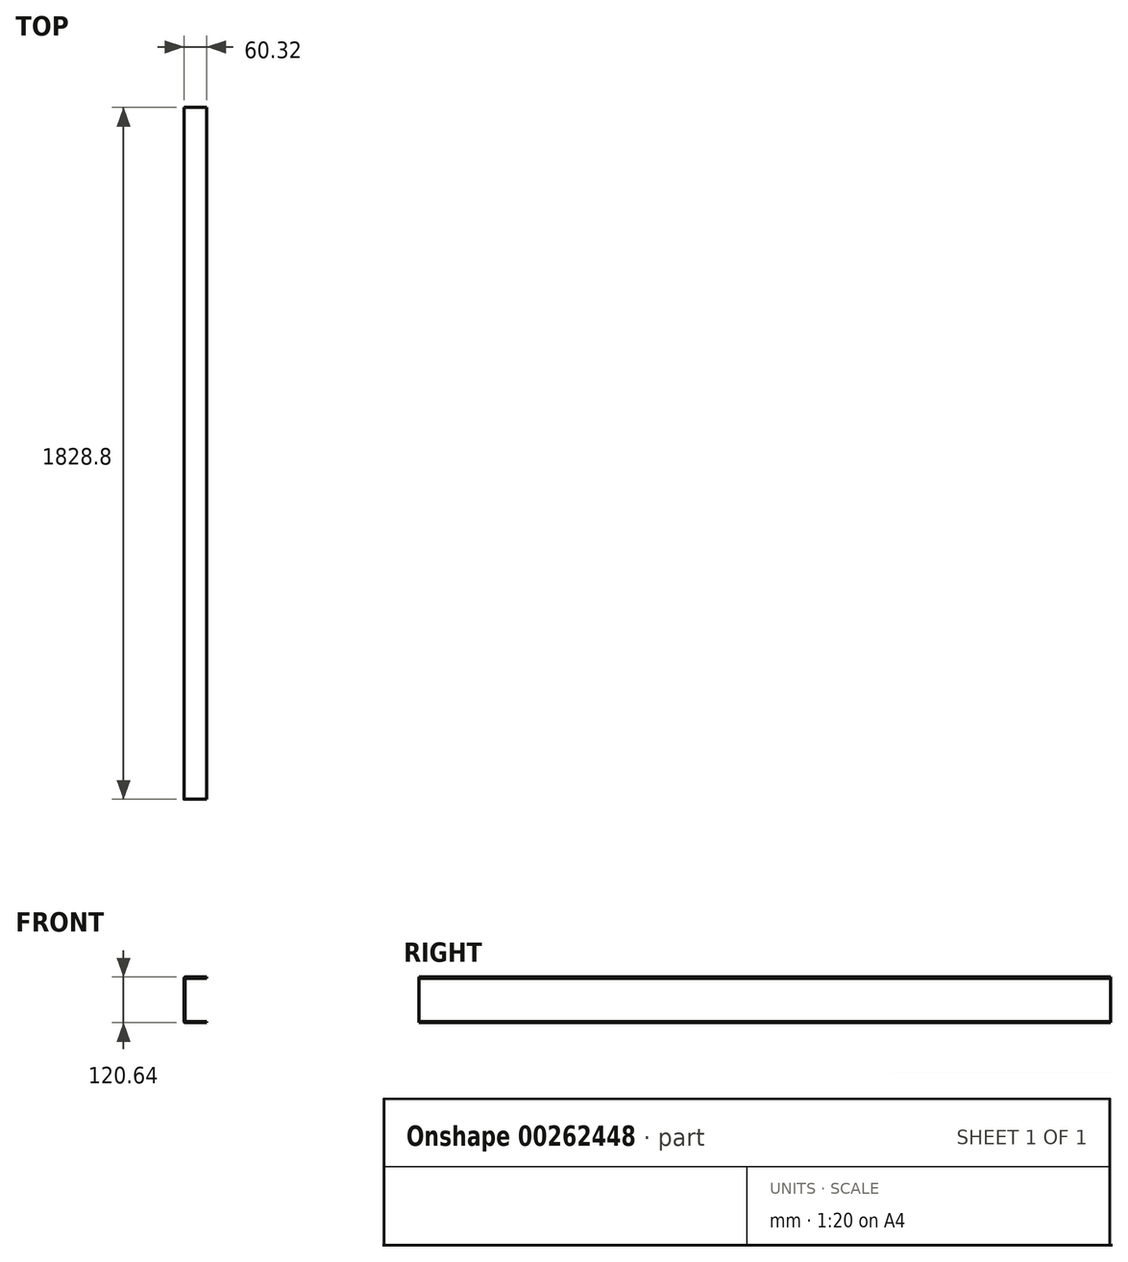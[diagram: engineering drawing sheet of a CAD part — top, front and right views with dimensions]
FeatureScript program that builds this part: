
annotation { "Feature Type Name" : "Feature", "Feature Type Description" : "" }
export const myFeature = defineFeature(function(context is Context, id is Id, definition is map)
    precondition{}
    {
        {
            var Q0;
            Q0=qCreatedBy(makeId("Front.planeOp"),FACE);
            var sketch = newSketch(context, id + "F0", { "sketchPlane" : qUnion([Q0])});
            skLineSegment(sketch, "E0.bottom", {"start": v(30.16, 60.33) * mm, "end": v(-26.99, 60.33) * mm});
            skLineSegment(sketch, "E0.top", {"start": v(30.16, -60.32) * mm, "end": v(-26.99, -60.32) * mm});
            skLineSegment(sketch, "E0.left", {"start": v(30.16, 60.33) * mm, "end": v(30.16, -60.32) * mm});
            skLineSegment(sketch, "E0.right", {"start": v(-30.16, 57.15) * mm, "end": v(-30.16, -57.15) * mm});
            skPoint(sketch, "E0.middle", {"position": v(0, 0) * mm});
            skLineSegment(sketch, "E1.bottom", {"start": v(30.16, 57.15) * mm, "end": v(-26.99, 57.15) * mm});
            skLineSegment(sketch, "E1.top", {"start": v(30.16, -57.15) * mm, "end": v(-26.99, -57.15) * mm});
            skLineSegment(sketch, "E1.left", {"start": v(30.16, 57.15) * mm, "end": v(30.16, -57.15) * mm});
            skLineSegment(sketch, "E1.right", {"start": v(-26.99, 57.15) * mm, "end": v(-26.99, -57.15) * mm});
            skPoint(sketch, "E2.visualSharp", {"position": v(-30.16, 60.33) * mm});
            skArc(sketch, "E2.filletArc", {"start": v(-26.99, 60.33) * mm, "mid": v(-29.23, 59.4) * mm, "end": v(-30.16, 57.15) * mm});
            skPoint(sketch, "E3.visualSharp", {"position": v(-30.16, -60.32) * mm});
            skArc(sketch, "E3.filletArc", {"start": v(-30.16, -57.15) * mm, "mid": v(-29.23, -59.4) * mm, "end": v(-26.99, -60.33) * mm});
            skSolve(sketch);
        }
        {
            var Q0;
            {var subQ4=sQuery(id+"F0.wireOp",EDGE,"E0.bottom");Q0=makeQuery(id+"F0.imprint","IMPRINT",FACE,{"disambiguationData":[TD([[makeQuery(id+"F0.imprint","IMPRINT",EDGE,{"derivedFrom":subQ4}),1.0]])]});}
            extrude(context, id + "F1", {"entities" : qUnion([Q0]), "depth" : 1828.8 * mm});
        }
    });
